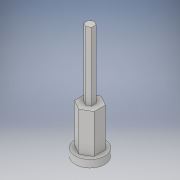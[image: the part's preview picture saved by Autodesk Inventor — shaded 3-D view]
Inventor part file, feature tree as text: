
AUTODESK INVENTOR PART (.ipt)
format: ipt  version: 2019 (Build 230136000, 136)  size: 118,784 bytes
history: native  units: in
note: dims shown in document units (in); Inventor stores cm internally (conversion verified against a paired STEP export)
features: extrude x3, sketch x3
ambient origin geometry x8: Origin, YZ Plane, XZ Plane, XY Plane, X Axis, Y Axis, Z Axis, Center Point
bodies: Solid1 (feature_tree)
feature tree (6):
  extrude  "Extrusion1"  Depth=0.1875in TaperAngle=0.0deg
  extrude  "Extrusion2"  Depth=1.0in TaperAngle=0.0deg
  extrude  "Extrusion3"  Depth=1.75in TaperAngle=0.0deg
  sketch  "Sketch1"  dims[d0=0.75in d1=0.1875in d2=0.0in]
  sketch  "Sketch2"  dims[d3=0.5in d4=1.0in d5=0.0in]
  sketch  "Sketch3"  dims[d6=0.1969in d7=1.75in d8=0.0in]
